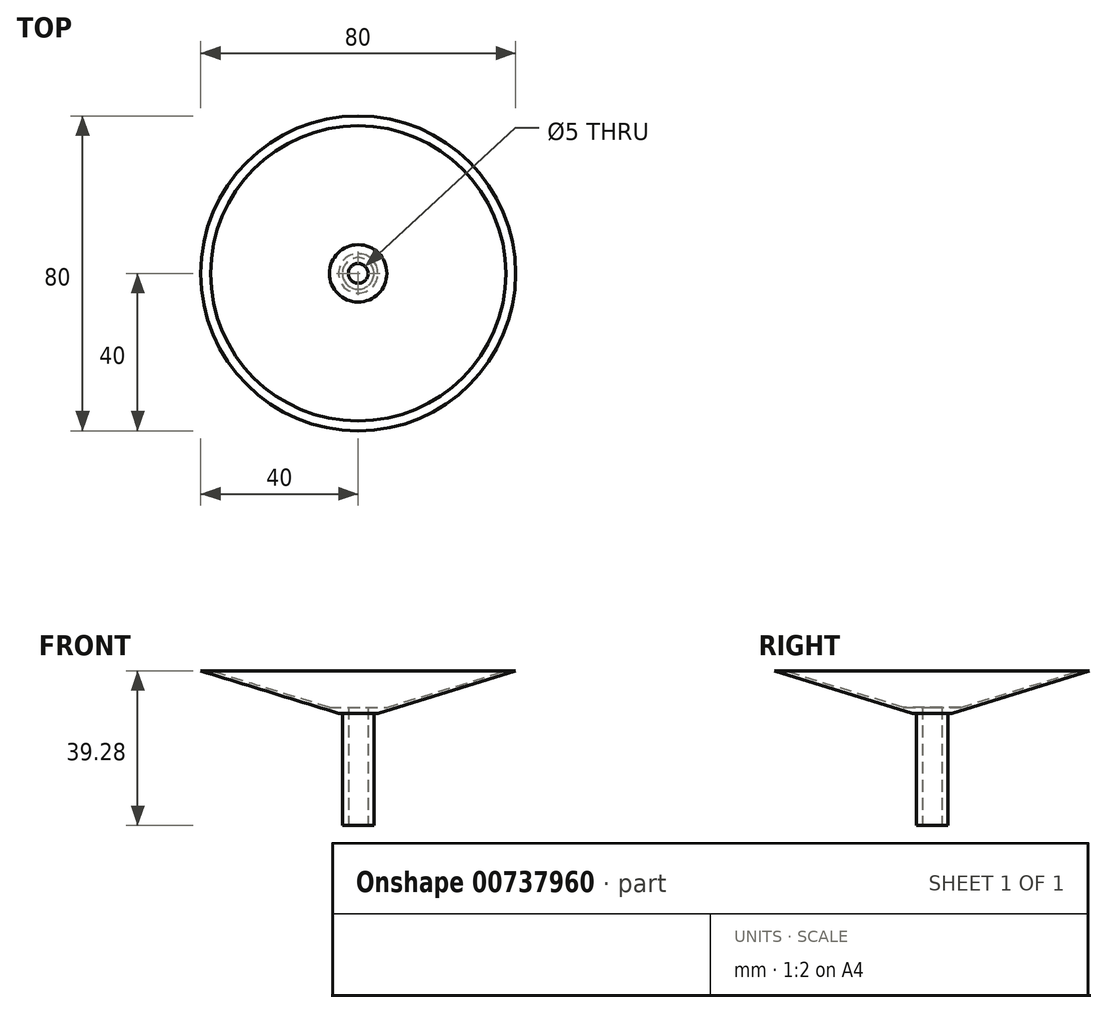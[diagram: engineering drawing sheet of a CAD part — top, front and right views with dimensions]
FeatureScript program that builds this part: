
annotation { "Feature Type Name" : "Feature", "Feature Type Description" : "" }
export const myFeature = defineFeature(function(context is Context, id is Id, definition is map)
    precondition{}
    {
        {
            var Q0;
            Q0=qCreatedBy(makeId("Front.planeOp"),FACE);
            var sketch = newSketch(context, id + "F0", { "sketchPlane" : qUnion([Q0])});
            skLineSegment(sketch, "E0", {"start": v(0, 0) * mm, "end": v(-5, 0) * mm});
            skLineSegment(sketch, "E1", {"start": v(-5, 0) * mm, "end": v(-40, 10.75) * mm});
            skLineSegment(sketch, "E2", {"start": v(-40, 10.75) * mm, "end": v(0, 10.75) * mm});
            skLineSegment(sketch, "E3", {"start": v(0, 10.75) * mm, "end": v(0, 0) * mm});
            skLineSegment(sketch, "E4", {"start": v(0, 0) * mm, "end": v(0, 6.25) * mm});
            skLineSegment(sketch, "E5", {"start": v(-37.5, 10.75) * mm, "end": v(-2.5, 0) * mm});
            skLineSegment(sketch, "E6", {"start": v(0, 1.47) * mm, "end": v(-7.28, 1.47) * mm});
            skLineSegment(sketch, "E7", {"start": v(-7.28, 1.47) * mm, "end": v(-9.78, 1.47) * mm});
            skSolve(sketch);
        }
        {
            var Q0;
            {var subQ5=sQuery(id+"F0.wireOp",EDGE,"E6");Q0=makeQuery(id+"F0.imprint","IMPRINT",FACE,{"disambiguationData":[TD([[makeQuery(id+"F0.imprint","IMPRINT",EDGE,{"derivedFrom":subQ5}),1.0]])]});}
            var Q1;
            {var subQ5=sQuery(id+"F0.wireOp",EDGE,"E7");Q1=makeQuery(id+"F0.imprint","IMPRINT",FACE,{"disambiguationData":[TD([[makeQuery(id+"F0.imprint","IMPRINT",EDGE,{"derivedFrom":subQ5}),1.0]])]});}
            var Q2;
            {var subQ3=sQuery(id+"F0.wireOp",EDGE,"E7");Q2=makeQuery(id+"F0.imprint","IMPRINT",FACE,{"disambiguationData":[TD([[makeQuery(id+"F0.imprint","IMPRINT",EDGE,{"derivedFrom":subQ3}),-1.0]])]});}
            var Q3;
            Q3=sQuery(id+"F0.wireOp",EDGE,"E4");
            revolve(context, id + "F1", {"surfaceOperationType" : NewSurfaceOperationType.NEW, "entities" : qUnion([Q0, Q1, Q2]), "axis" : qUnion([Q3]), "revolveType" : RevolveType.FULL});
        }
        {
            var Q0;
            Q0=makeQuery(id+"F1.opRevolve","SWEPT_FACE",FACE,{"disambiguationData":[OSD([sQuery(id+"F0.wireOp",EDGE,"E6")])]});
            var sketch = newSketch(context, id + "F2", { "sketchPlane" : qUnion([Q0])});
            skCircle(sketch, "E8", {"center": v(0, 0) * mm, "radius": 4 * mm});
            skSolve(sketch);
        }
        {
            var Q0;
            Q0 = qSketchRegion(id + "F2", true);
            extrude(context, id + "F3", {"entities" : qUnion([Q0]), "operationType" : NewBodyOperationType.ADD, "oppositeDirection" : true, "depth" : 30 * mm, "offsetDistance" : 25 * mm});
        }
        {
            var Q0;
            Q0=makeQuery(id+"F3.opExtrude","CAP_FACE",FACE,{"disambiguationData":[OSD([sQuery(id+"F2.wireOp",EDGE,"E8")])],"isStart":false});
            var sketch = newSketch(context, id + "F4", { "sketchPlane" : qUnion([Q0])});
            skSolve(sketch);
        }
        {
            var Q0;
            Q0=makeQuery(id+"F4.imprint","IMPRINT",FACE,{"disambiguationData":[TD([[makeQuery(id+"F4.imprint","IMPRINT",EDGE,{"derivedFrom":makeQuery(id+"F3.opExtrude","CAP_EDGE",EDGE,{"disambiguationData":[OSD([sQuery(id+"F2.wireOp",EDGE,"E8")])],"isStart":false})}),-1.0]])]});
            var sketch = newSketch(context, id + "F5", { "sketchPlane" : qUnion([Q0])});
            skCircle(sketch, "E9", {"center": v(0, 0) * mm, "radius": 2.5 * mm});
            skSolve(sketch);
        }
        {
            var Q0;
            Q0=makeQuery(id+"F5.imprint","IMPRINT",FACE,{"disambiguationData":[TD([[makeQuery(id+"F5.imprint","IMPRINT",EDGE,{"derivedFrom":sQuery(id+"F5.wireOp",EDGE,"E9")}),1.0]])]});
            extrude(context, id + "F6", {"entities" : qUnion([Q0]), "operationType" : NewBodyOperationType.REMOVE, "oppositeDirection" : true, "depth" : 50 * mm, "offsetDistance" : 25 * mm});
        }
    });
